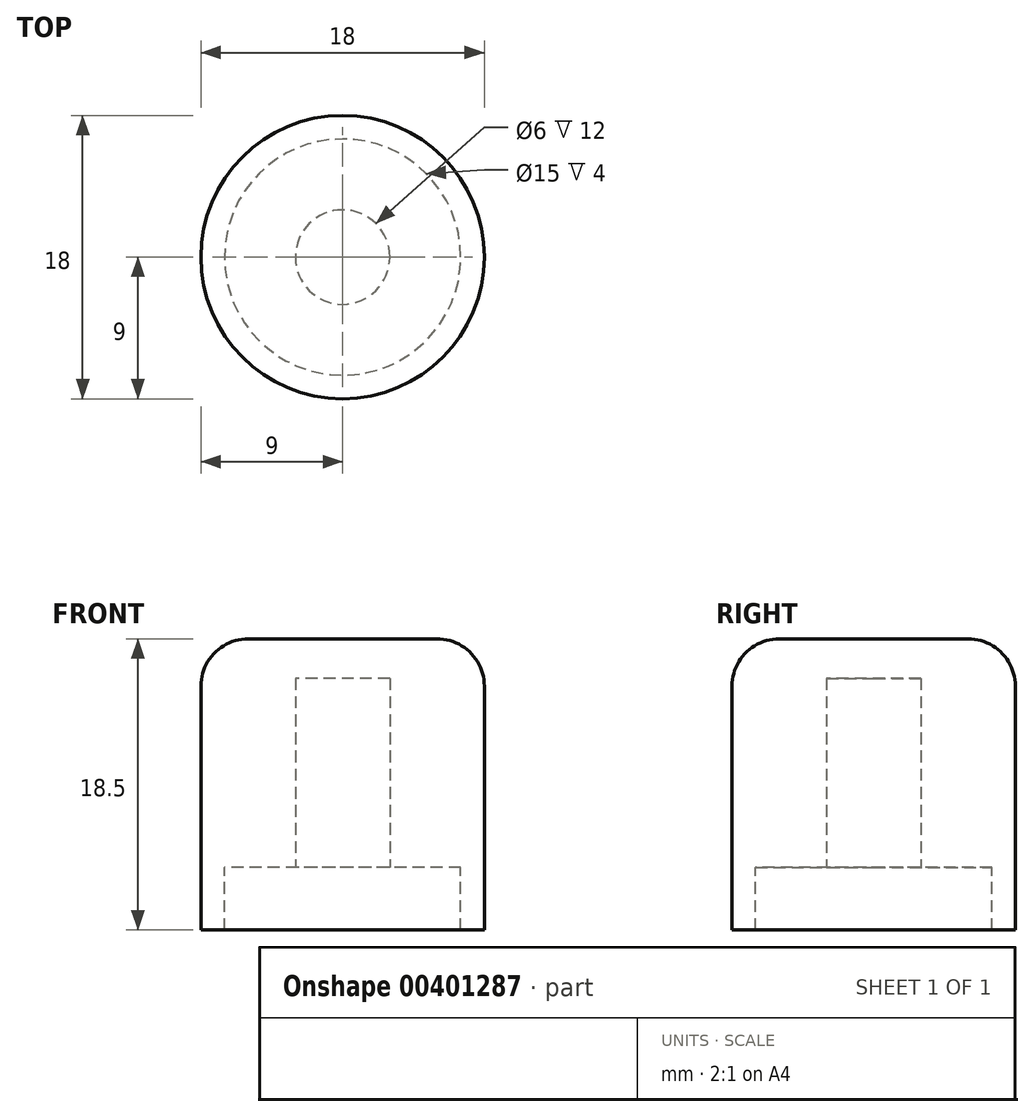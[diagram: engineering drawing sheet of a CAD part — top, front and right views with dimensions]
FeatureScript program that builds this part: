
annotation { "Feature Type Name" : "Feature", "Feature Type Description" : "" }
export const myFeature = defineFeature(function(context is Context, id is Id, definition is map)
    precondition{}
    {
        {
            var Q0;
            Q0=qCreatedBy(makeId("Top.planeOp"),FACE);
            var sketch = newSketch(context, id + "F0", { "sketchPlane" : qUnion([Q0])});
            skCircle(sketch, "E0", {"center": v(0, 0) * mm, "radius": 3 * mm});
            skCircle(sketch, "E1", {"center": v(0, 0) * mm, "radius": 9 * mm});
            skLineSegment(sketch, "E2", {"start": v(1.5, 2.6) * mm, "end": v(1.5, -2.6) * mm});
            skCircle(sketch, "E3", {"center": v(0, 0) * mm, "radius": 7.5 * mm});
            skSolve(sketch);
        }
        {
            var Q0;
            Q0=makeQuery(id+"F0.imprint","IMPRINT",FACE,{"disambiguationData":[TD([[makeQuery(id+"F0.imprint","IMPRINT",EDGE,{"derivedFrom":sQuery(id+"F0.wireOp",EDGE,"E3")}),1.0]])]});
            var Q1;
            Q1=makeQuery(id+"F0.imprint","IMPRINT",FACE,{"disambiguationData":[TD([[makeQuery(id+"F0.imprint","IMPRINT",EDGE,{"derivedFrom":sQuery(id+"F0.wireOp",EDGE,"E1")}),1.0]])]});
            var Q2;
            {var subQ0=sQuery(id+"F0.wireOp",EDGE,"E2");Q2=makeQuery(id+"F0.imprint","IMPRINT",FACE,{"disambiguationData":[TD([[makeQuery(id+"F0.imprint","IMPRINT",EDGE,{"derivedFrom":subQ0}),-1.0]])]});}
            var Q3;
            {var subQ0=sQuery(id+"F0.wireOp",EDGE,"E2");Q3=makeQuery(id+"F0.imprint","IMPRINT",FACE,{"disambiguationData":[TD([[makeQuery(id+"F0.imprint","IMPRINT",EDGE,{"derivedFrom":subQ0}),1.0]])]});}
            extrude(context, id + "F1", {"entities" : qUnion([Q0, Q1, Q2, Q3]), "offsetDistance" : 25 * mm, "depth" : 14.5 * mm});
        }
        {
            var Q0;
            {var subQ0=sQuery(id+"F0.wireOp",EDGE,"E2");Q0=makeQuery(id+"F0.imprint","IMPRINT",FACE,{"disambiguationData":[TD([[makeQuery(id+"F0.imprint","IMPRINT",EDGE,{"derivedFrom":subQ0}),-1.0]])]});}
            var Q1;
            {var subQ0=sQuery(id+"F0.wireOp",EDGE,"E2");Q1=makeQuery(id+"F0.imprint","IMPRINT",FACE,{"disambiguationData":[TD([[makeQuery(id+"F0.imprint","IMPRINT",EDGE,{"derivedFrom":subQ0}),1.0]])]});}
            extrude(context, id + "F2", {"entities" : qUnion([Q0, Q1]), "operationType" : NewBodyOperationType.REMOVE, "offsetDistance" : 25 * mm, "depth" : 12 * mm});
        }
        {
            var Q0;
            Q0=makeQuery(id+"F0.imprint","IMPRINT",FACE,{"disambiguationData":[TD([[makeQuery(id+"F0.imprint","IMPRINT",EDGE,{"derivedFrom":sQuery(id+"F0.wireOp",EDGE,"E1")}),1.0]])]});
            extrude(context, id + "F3", {"entities" : qUnion([Q0]), "operationType" : NewBodyOperationType.ADD, "oppositeDirection" : true, "depth" : 4 * mm});
        }
        {
            var Q0;
            Q0=makeQuery(id+"F1.opExtrude","CAP_EDGE",EDGE,{"disambiguationData":[OSD([sQuery(id+"F0.wireOp",EDGE,"E1")])],"isStart":false});
            fillet(context, id + "F4", {"entities" : qUnion([Q0]), "radius" : 3 * mm, "tangentPropagation" : true, "allowEdgeOverflow" : false});
        }
    });
